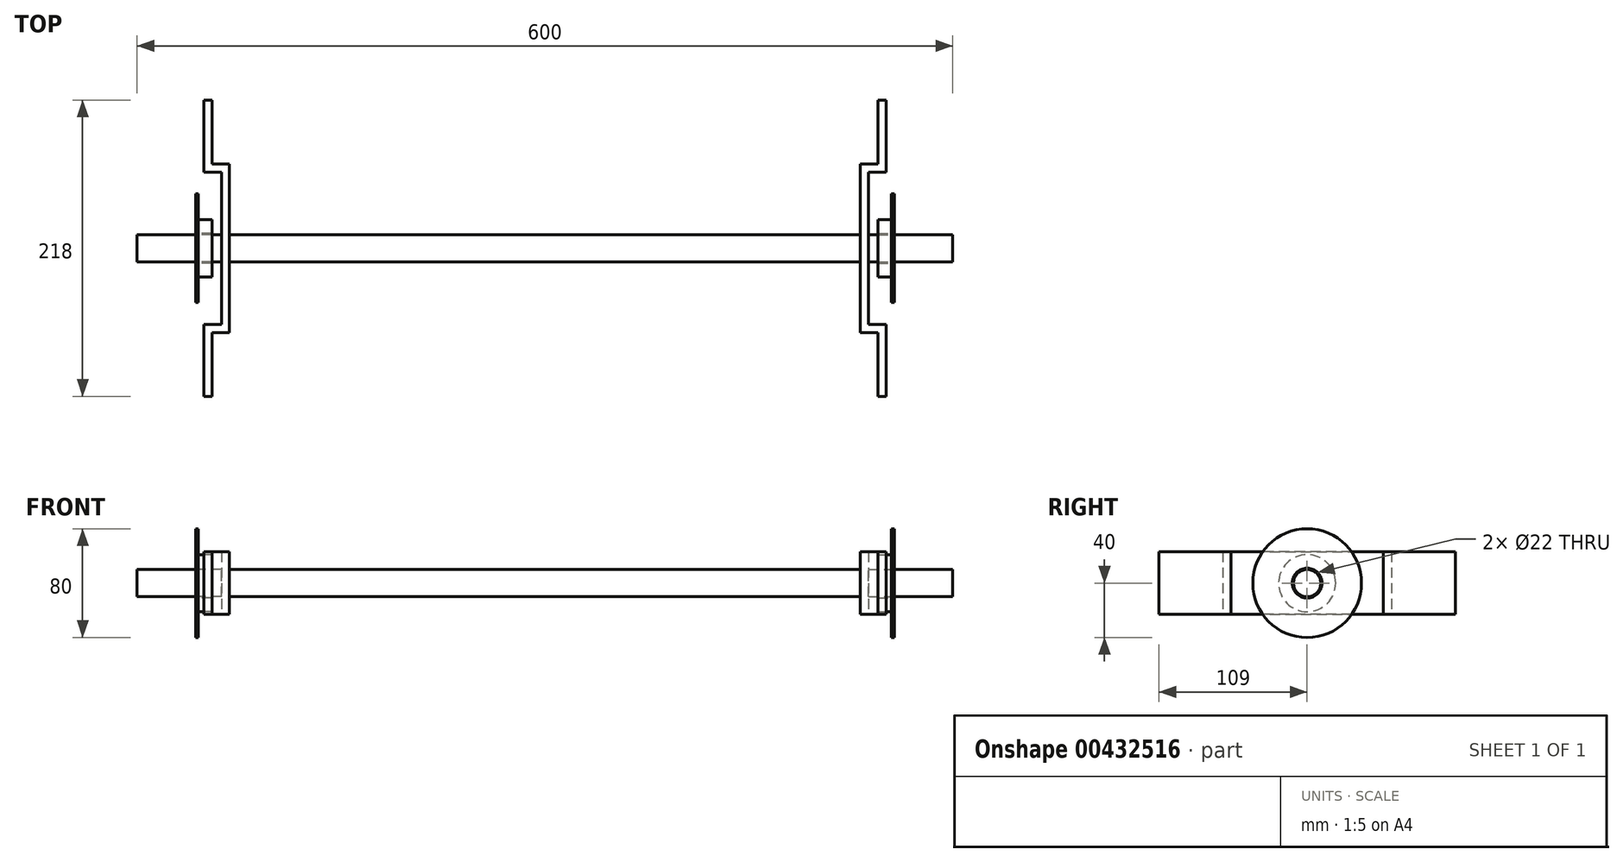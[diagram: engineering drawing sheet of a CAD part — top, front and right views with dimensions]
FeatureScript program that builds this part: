
annotation { "Feature Type Name" : "Feature", "Feature Type Description" : "" }
export const myFeature = defineFeature(function(context is Context, id is Id, definition is map)
    precondition{}
    {
        {
            assignVariable(context, id + "F0", {"name" : "b", "anyValue" : 300});
        }
        {
            var Q0;
            Q0=qCreatedBy(makeId("Right.planeOp"),FACE);
            cPlane(context, id + "F1", {"entities" : qUnion([Q0]), "cplaneType" : CPlaneType.OFFSET, "offset" : (getVariable(context, 'b')) * mm, "width" : 150 * mm, "height" : 150 * mm});
        }
        {
            var Q0;
            Q0=qCreatedBy(id+"F1.planeOp",FACE);
            var sketch = newSketch(context, id + "F2", { "sketchPlane" : qUnion([Q0])});
            skPoint(sketch, "E0.0", {"position": v(0, 0) * mm});
            skCircle(sketch, "E1", {"center": v(0, 0) * mm, "radius": 90 * mm, "construction": true});
            skCircle(sketch, "E2", {"center": v(0, 0) * mm, "radius": 10 * mm});
            skLineSegment(sketch, "E3.bottom", {"start": v(85.15, 14.51) * mm, "end": v(-85.15, 14.51) * mm});
            skLineSegment(sketch, "E3.top", {"start": v(85.15, -14.51) * mm, "end": v(-85.15, -14.51) * mm});
            skLineSegment(sketch, "E3.left", {"start": v(85.15, 14.51) * mm, "end": v(85.15, -14.51) * mm});
            skLineSegment(sketch, "E3.right", {"start": v(-85.15, 14.51) * mm, "end": v(-85.15, -14.51) * mm});
            skCircle(sketch, "E4", {"center": v(0, 0) * mm, "radius": 86.37 * mm, "construction": true});
            skSolve(sketch);
        }
        {
            var Q0;
            Q0=makeQuery(id+"F2.imprint","IMPRINT",FACE,{"disambiguationData":[TD([[makeQuery(id+"F2.imprint","IMPRINT",EDGE,{"derivedFrom":sQuery(id+"F2.wireOp",EDGE,"E2")}),1.0]])]});
            extrude(context, id + "F3", {"entities" : qUnion([Q0]), "oppositeDirection" : true, "depth" : (getVariable(context, 'b')) * mm});
        }
        {
            var Q0;
            Q0=qCreatedBy(makeId("Top.planeOp"),FACE);
            var sketch = newSketch(context, id + "F4", { "sketchPlane" : qUnion([Q0])});
            skLineSegment(sketch, "E5", {"start": v(0, 10) * mm, "end": v(300, 10) * mm, "construction": true});
            skLineSegment(sketch, "E6", {"start": v(300, -10) * mm, "end": v(238, -10) * mm, "construction": true});
            skLineSegment(sketch, "E7.0", {"start": v(300, 10) * mm, "end": v(300, -10) * mm, "construction": true});
            skLineSegment(sketch, "E8", {"start": v(300, 0) * mm, "end": v(162.54, 0) * mm, "construction": true});
            skLineSegment(sketch, "E9", {"start": v(257, -11) * mm, "end": v(245, -11) * mm});
            skLineSegment(sketch, "E10", {"start": v(257, -11) * mm, "end": v(257, -40) * mm});
            skLineSegment(sketch, "E11", {"start": v(257, -40) * mm, "end": v(255, -40) * mm});
            skLineSegment(sketch, "E12", {"start": v(255, -40) * mm, "end": v(255, -21) * mm});
            skLineSegment(sketch, "E13", {"start": v(255, -21) * mm, "end": v(245, -21) * mm});
            skLineSegment(sketch, "E14", {"start": v(245, -21) * mm, "end": v(245, -11) * mm});
            skLineSegment(sketch, "E15", {"start": v(238, -10) * mm, "end": v(238, -56) * mm});
            skLineSegment(sketch, "E16", {"start": v(238, -62) * mm, "end": v(232, -62) * mm});
            skLineSegment(sketch, "E17", {"start": v(232, -62) * mm, "end": v(232, -10) * mm});
            skLineSegment(sketch, "E18", {"start": v(251, -56) * mm, "end": v(251, -109) * mm});
            skLineSegment(sketch, "E19", {"start": v(251, -56) * mm, "end": v(238, -56) * mm});
            skLineSegment(sketch, "E20", {"start": v(245, -109) * mm, "end": v(245, -62) * mm});
            skLineSegment(sketch, "E21", {"start": v(245, -62) * mm, "end": v(238, -62) * mm});
            skLineSegment(sketch, "E22", {"start": v(245, -109) * mm, "end": v(251, -109) * mm});
            skLineSegment(sketch, "E23", {"start": v(232, -10) * mm, "end": v(232, 0) * mm});
            skLineSegment(sketch, "E24", {"start": v(232, 0) * mm, "end": v(238, 0) * mm});
            skLineSegment(sketch, "E25", {"start": v(238, 0) * mm, "end": v(238, -10) * mm});
            skLineSegment(sketch, "E26.trimOffspring", {"start": v(232, -10) * mm, "end": v(0, -10) * mm, "construction": true});
            skSolve(sketch);
        }
        {
            var Q0;
            Q0=makeQuery(id+"F4.imprint","IMPRINT",FACE,{"disambiguationData":[TD([[makeQuery(id+"F4.imprint","IMPRINT",EDGE,{"derivedFrom":sQuery(id+"F4.wireOp",EDGE,"E9")}),1.0]])]});
            var Q1;
            Q1=sQuery(id+"F4.wireOp",EDGE,"E8");
            revolve(context, id + "F5", {"entities" : qUnion([Q0]), "axis" : qUnion([Q1]), "revolveType" : RevolveType.FULL});
        }
        {
            var Q0;
            Q0=makeQuery(id+"F4.imprint","IMPRINT",FACE,{"disambiguationData":[TD([[makeQuery(id+"F4.imprint","IMPRINT",EDGE,{"derivedFrom":sQuery(id+"F4.wireOp",EDGE,"E15")}),-1.0]])]});
            extrude(context, id + "F6", {"entities" : qUnion([Q0]), "depth" : 23 * mm, "hasSecondDirection" : true, "secondDirectionOppositeDirection" : true, "secondDirectionDepth" : 23 * mm});
        }
        {
            var Q0;
            Q0=makeQuery(id+"F6.opExtrude","SWEPT_BODY",BODY,{"disambiguationData":[OSD([sQuery(id+"F4.wireOp",EDGE,"E15"),sQuery(id+"F4.wireOp",EDGE,"E16"),sQuery(id+"F4.wireOp",EDGE,"E17"),sQuery(id+"F4.wireOp",EDGE,"E18"),sQuery(id+"F4.wireOp",EDGE,"E19"),sQuery(id+"F4.wireOp",EDGE,"E20"),sQuery(id+"F4.wireOp",EDGE,"E21"),sQuery(id+"F4.wireOp",EDGE,"E22"),sQuery(id+"F4.wireOp",EDGE,"E23"),sQuery(id+"F4.wireOp",EDGE,"E24"),sQuery(id+"F4.wireOp",EDGE,"E25")])]});
            var Q1;
            Q1=makeQuery(id+"F6.opExtrude","SWEPT_FACE",FACE,{"disambiguationData":[OSD([sQuery(id+"F4.wireOp",EDGE,"E24")])]});
            mirror(context, id + "F7", {"operationType" : NewBodyOperationType.ADD, "entities" : qUnion([Q0]), "mirrorPlane" : qUnion([Q1])});
        }
        {
            var Q0;
            Q0=makeQuery(id+"F3.opExtrude","SWEPT_BODY",BODY,{"disambiguationData":[OSD([sQuery(id+"F2.wireOp",EDGE,"E2")])]});
            var Q1;
            Q1=makeQuery(id+"F5.opRevolve","SWEPT_BODY",BODY,{"disambiguationData":[OSD([sQuery(id+"F4.wireOp",EDGE,"E9"),sQuery(id+"F4.wireOp",EDGE,"E10"),sQuery(id+"F4.wireOp",EDGE,"E11"),sQuery(id+"F4.wireOp",EDGE,"E12"),sQuery(id+"F4.wireOp",EDGE,"E13"),sQuery(id+"F4.wireOp",EDGE,"E14")])]});
            var Q2;
            Q2=qCreatedBy(makeId("Right.planeOp"),FACE);
            mirror(context, id + "F8", {"operationType" : NewBodyOperationType.ADD, "entities" : qUnion([Q0, Q1]), "mirrorPlane" : qUnion([Q2])});
        }
    });
